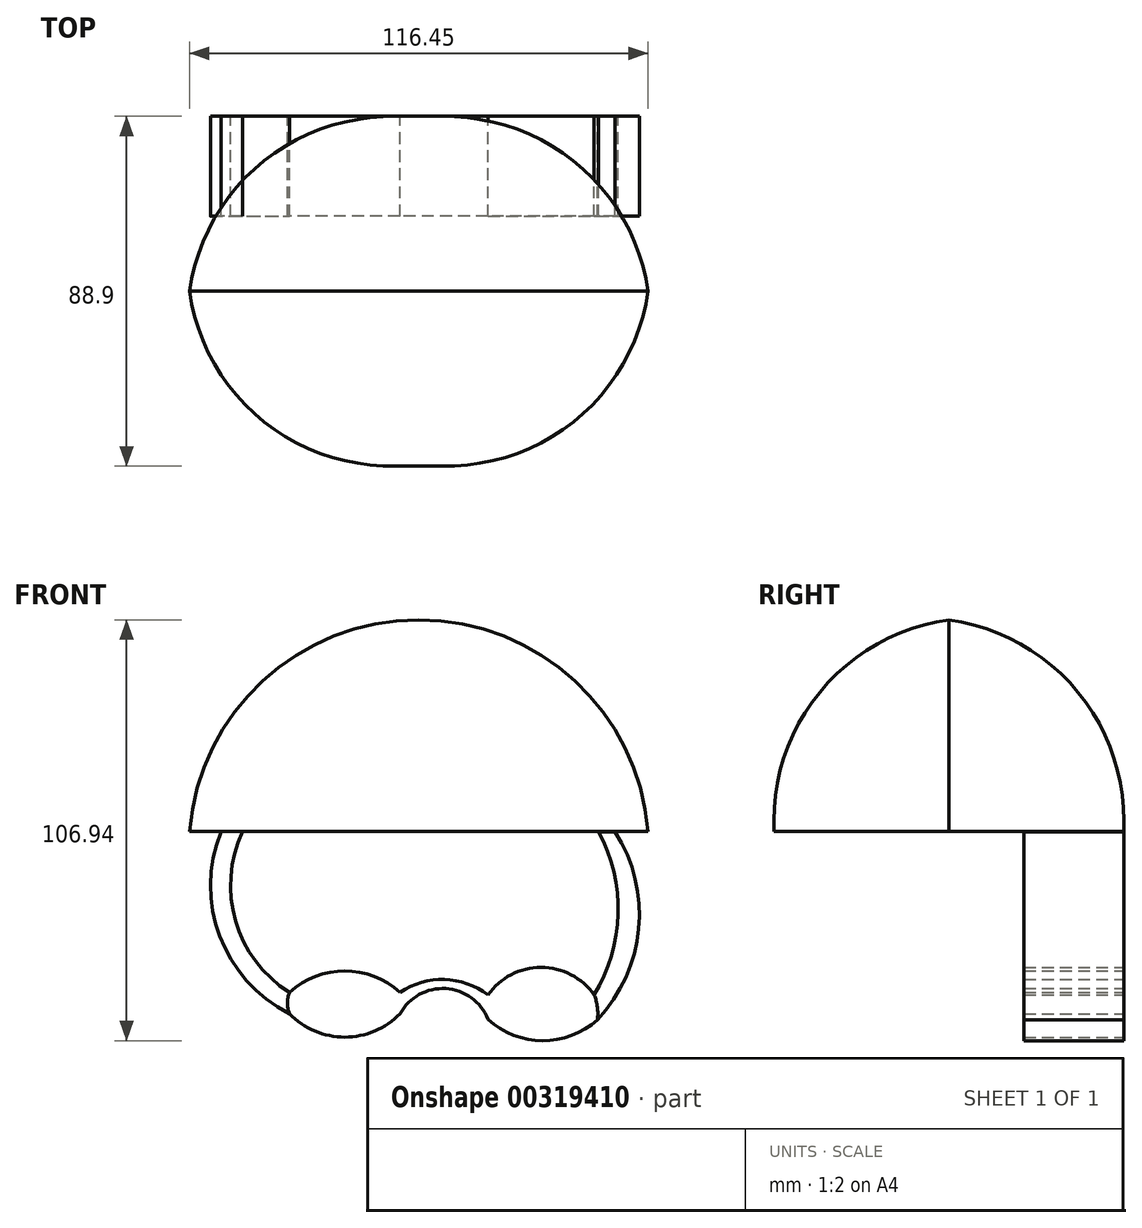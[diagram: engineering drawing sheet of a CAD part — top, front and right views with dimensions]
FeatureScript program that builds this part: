
annotation { "Feature Type Name" : "Feature", "Feature Type Description" : "" }
export const myFeature = defineFeature(function(context is Context, id is Id, definition is map)
    precondition{}
    {
        {
            var Q0;
            Q0=qCreatedBy(makeId("Front.planeOp"),FACE);
            var sketch = newSketch(context, id + "F0", { "sketchPlane" : qUnion([Q0])});
            skLineSegment(sketch, "E0", {"start": v(-57.85, 19.86) * mm, "end": v(59.58, 19.86) * mm});
            skArc(sketch, "E1", {"start": v(59.58, 19.86) * mm, "mid": v(0.86, 74.17) * mm, "end": v(-57.85, 19.86) * mm});
            skSolve(sketch);
        }
        {
            var Q0;
            Q0=makeQuery(id+"F0.imprint","IMPRINT",FACE,{"disambiguationData":[TD([[makeQuery(id+"F0.imprint","IMPRINT",EDGE,{"derivedFrom":sQuery(id+"F0.wireOp",EDGE,"E0")}),1.0]])]});
            extrude(context, id + "F1", {"entities" : qUnion([Q0]), "depth" : 88.9 * mm});
        }
        {
            var Q0;
            Q0=makeQuery(id+"F1.opExtrude","CAP_EDGE",EDGE,{"disambiguationData":[OSD([sQuery(id+"F0.wireOp",EDGE,"E1")])],"isStart":false});
            var Q1;
            Q1=makeQuery(id+"F1.opExtrude","CAP_EDGE",EDGE,{"disambiguationData":[OSD([sQuery(id+"F0.wireOp",EDGE,"E1")])],"isStart":true});
            fillet(context, id + "F2", {"entities" : qUnion([Q0, Q1]), "radius" : 51.5 * mm, "tangentPropagation" : true, "allowEdgeOverflow" : false});
        }
        {
            var Q0;
            Q0=qCreatedBy(makeId("Front.planeOp"),FACE);
            var sketch = newSketch(context, id + "F3", { "sketchPlane" : qUnion([Q0])});
            skArc(sketch, "E2", {"start": v(-49.4, 19.8) * mm, "mid": v(-49.7, -6.7) * mm, "end": v(-31.97, -26.4) * mm});
            skArc(sketch, "E3", {"start": v(-43.9, 19.88) * mm, "mid": v(-45.68, -2.82) * mm, "end": v(-31.97, -21.01) * mm});
            skArc(sketch, "E4", {"start": v(-3.9, -21.01) * mm, "mid": v(-17.93, -15.6) * mm, "end": v(-31.97, -21.01) * mm});
            skArc(sketch, "E5", {"start": v(-31.97, -26.4) * mm, "mid": v(-17.93, -32.36) * mm, "end": v(-3.9, -26.4) * mm});
            skArc(sketch, "E6", {"start": v(-31.97, -21.01) * mm, "mid": v(-32.53, -23.7) * mm, "end": v(-31.97, -26.4) * mm});
            skArc(sketch, "E7", {"start": v(-3.9, -26.4) * mm, "mid": v(-3.12, -23.7) * mm, "end": v(-3.9, -21.01) * mm});
            skArc(sketch, "E8", {"start": v(46.23, -27.97) * mm, "mid": v(56.72, -4.85) * mm, "end": v(50.75, 19.84) * mm});
            skArc(sketch, "E9", {"start": v(45.42, -21.68) * mm, "mid": v(51.51, -1.07) * mm, "end": v(46.55, 19.84) * mm});
            skArc(sketch, "E10", {"start": v(45.42, -21.68) * mm, "mid": v(31.94, -14.62) * mm, "end": v(18.45, -21.68) * mm});
            skArc(sketch, "E11", {"start": v(18.45, -27.81) * mm, "mid": v(32.3, -33.26) * mm, "end": v(46.23, -27.97) * mm});
            skArc(sketch, "E12", {"start": v(46.23, -27.97) * mm, "mid": v(46.26, -24.77) * mm, "end": v(45.42, -21.68) * mm});
            skArc(sketch, "E13", {"start": v(18.45, -21.68) * mm, "mid": v(17.17, -24.74) * mm, "end": v(18.45, -27.81) * mm});
            skArc(sketch, "E14", {"start": v(18.45, -21.68) * mm, "mid": v(7.38, -17.72) * mm, "end": v(-3.9, -21.01) * mm});
            skArc(sketch, "E15", {"start": v(18.45, -27.81) * mm, "mid": v(7.72, -20.03) * mm, "end": v(-3.9, -26.4) * mm});
            skLineSegment(sketch, "E16", {"start": v(50.75, 19.84) * mm, "end": v(46.55, 19.84) * mm});
            skLineSegment(sketch, "E17", {"start": v(-43.9, 19.88) * mm, "end": v(-49.4, 19.8) * mm});
            skSolve(sketch);
        }
        {
            var Q0;
            {var subQ1=sQuery(id+"F3.wireOp",EDGE,"E4");Q0=makeQuery(id+"F3.imprint","IMPRINT",FACE,{"disambiguationData":[TD([[makeQuery(id+"F3.imprint","IMPRINT",EDGE,{"derivedFrom":subQ1}),1.0]])]});}
            var Q1;
            {var subQ1=sQuery(id+"F3.wireOp",EDGE,"E10");Q1=makeQuery(id+"F3.imprint","IMPRINT",FACE,{"disambiguationData":[TD([[makeQuery(id+"F3.imprint","IMPRINT",EDGE,{"derivedFrom":subQ1}),1.0]])]});}
            var Q2;
            {var subQ0=sQuery(id+"F3.wireOp",EDGE,"E14");Q2=makeQuery(id+"F3.imprint","IMPRINT",FACE,{"disambiguationData":[TD([[makeQuery(id+"F3.imprint","IMPRINT",EDGE,{"derivedFrom":subQ0}),1.0]])]});}
            extrude(context, id + "F4", {"entities" : qUnion([Q0, Q1, Q2]), "depth" : 25.4 * mm});
        }
        {
            var Q0;
            Q0=makeQuery(id+"F3.imprint","IMPRINT",FACE,{"disambiguationData":[TD([[makeQuery(id+"F3.imprint","IMPRINT",EDGE,{"derivedFrom":sQuery(id+"F3.wireOp",EDGE,"E2")}),1.0]])]});
            var Q1;
            Q1=makeQuery(id+"F3.imprint","IMPRINT",FACE,{"disambiguationData":[TD([[makeQuery(id+"F3.imprint","IMPRINT",EDGE,{"derivedFrom":sQuery(id+"F3.wireOp",EDGE,"E8")}),1.0]])]});
            extrude(context, id + "F5", {"entities" : qUnion([Q0, Q1]), "depth" : 25.4 * mm});
        }
    });
